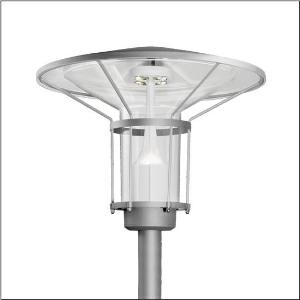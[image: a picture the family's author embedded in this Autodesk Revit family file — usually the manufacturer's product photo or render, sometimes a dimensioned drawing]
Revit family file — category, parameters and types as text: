
# Revit family: laterne_classic_iq___st1_2a_5xa5245af14h_9f1a
name_source: partatom
category: Lighting Fixtures
units: mm (PartAtom-declared; Revit-internal decimal feet)

## family parameters
Cut with Voids When Loaded = No
Host = Face
Light Source = No
Part Type = Normal
Room Calculation Point = No
Round Connector Dimension = Use Diameter
Shared = No

## types (1)
- --- (1 x LED, 1380 lm, 12.9 W, 2200K)
    Apparent Load = 13 VA
    CIE Flux Codes = 21 60 93 97 100
    Color Rendering = 70
    Color Temperature = 2200K
    Default Elevation = 1800 mm
    Description = Lantern Classic iQ, mast luminaire, Module 540 iQ-SR, primary light control with 3 zone facetted reflector, of plastic, silver coated, highly specular, structured, primary optical cover: cover, of PMMA, transparent, light distribution: ST1.2a, light emission: direct distribution, primary light characteristic: asymmetric, installation type: post-top, LED, High Power LED, rated luminous flux: 1.380lm, luminous efficacy: 107lm/W, light colour: 722, colour temperature: 2200K, control gear: ECG iQ, control: presetting dimming logarithmic, Street-Remote, Auto-Match, Temp-Guard, Lumen-Switch, Night-Set, Smart-Wire, Light-Fading, Desk-Remote (wireless, voltage-free reading and setting of iQ features in the workshop via application-optimized NFC function/RFID function), optimised constant luminous flux control (CLO 2.0), with terminal, 6-pole, max. 2.5mm², mains connection: 230..240V, AC, 50/60Hz, start of lifetime: 13W, end of service life: 13W, reduction: 6W, luminaire housing, upper part, of glass-fibre reinforced polyester, coated, Siteco® metallic grey (DB 702S), diameter: 750mm, height: 596mm, spigot size: d x l = 76 x 70mm (post-top) | with reducer (optional accessory) 60 x 70mm, post-top mast mounting element, of diecast aluminium, coated, Siteco® metallic grey (DB 702S), Module 540 iQ-SR, traffic white (RAL 9016), equipment: standard, protection rating (complete): IP65, insulation class (complete): insulation class II (safety insulation), certification: CE, ENEC, VDE, packaging unit: 1 piece

Light Distribution: ST1.2a
    Height = 596 mm
    Lamp = 1 x LED
    Lamp Light Flux = 1380 lm
    Lamp Power = 12.9 W
    Lamp count = 1
    Length = 750 mm
    Luminous efficacy = 107 lm/W
    Manufacturer = Siteco
    ModVariant = No
    Model = 5XA5245AF14H
    Number of Poles = 1
    OnlyDefault = Yes
    Power Factor = 1
    Product Name = Laterne Classic iQ | ST1.2a
    Product group = mast luminaire | pylon top
    ProductGroupID = 6100
    Protection Class = Protection class II
    Protection Degree = IP 65
    RLX_Detail_Level = 1
    RLX_Emergency_Light_Flux = 0 lm
    RLX_Emergency_Type = 0
    RLX_Emergency_Type_DB = No
    RlxData = <blob elided: 92057 chars, md5=4c8a4b41>
    Socket = socket
    Standby Power = 0 W
    System Light Flux = 1380 lm
    System Power = 13 W
    Type Comments = factory setting: luminous flux: 100 % | dim-lin: 254 | 516 mA
    Type Image = l_1006052.jpg
    URL = http://relux.com
    VarID = @adj_092731
    Voltage = 0 V
    Weight = 0.00 kg
    Width = 0 mm  [stored 0 ft]

note: [stored X ft] marks values corroborated as IEEE doubles in the binary element streams (Revit-internal decimal feet)

## geometry (parser evidence)
native form markers: Blend x4, Sweep x10
no freeform markers — native parametric forms only
